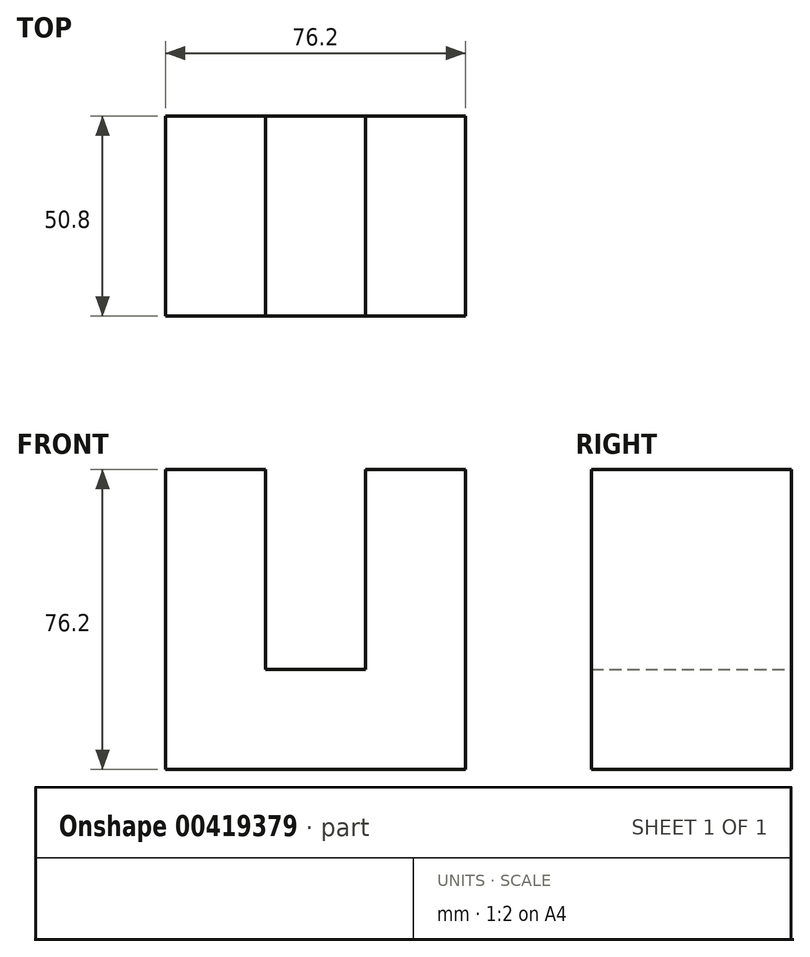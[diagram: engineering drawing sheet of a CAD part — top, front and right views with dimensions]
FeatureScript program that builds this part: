
annotation { "Feature Type Name" : "Feature", "Feature Type Description" : "" }
export const myFeature = defineFeature(function(context is Context, id is Id, definition is map)
    precondition{}
    {
        {
            var Q0;
            Q0=qCreatedBy(makeId("Front.planeOp"),FACE);
            var sketch = newSketch(context, id + "F0", { "sketchPlane" : qUnion([Q0])});
            skLineSegment(sketch, "E0", {"start": v(0, 0) * mm, "end": v(76.2, 0) * mm});
            skLineSegment(sketch, "E1", {"start": v(0, 0) * mm, "end": v(0, 76.2) * mm});
            skLineSegment(sketch, "E2", {"start": v(0, 76.2) * mm, "end": v(25.4, 76.2) * mm});
            skLineSegment(sketch, "E3", {"start": v(25.4, 76.2) * mm, "end": v(25.4, 25.4) * mm});
            skLineSegment(sketch, "E4", {"start": v(76.2, 0) * mm, "end": v(76.2, 76.2) * mm});
            skLineSegment(sketch, "E5", {"start": v(76.2, 76.2) * mm, "end": v(50.8, 76.2) * mm});
            skLineSegment(sketch, "E6", {"start": v(50.8, 76.2) * mm, "end": v(50.8, 25.4) * mm});
            skLineSegment(sketch, "E7", {"start": v(25.4, 25.4) * mm, "end": v(50.8, 25.4) * mm});
            skSolve(sketch);
        }
        {
            var Q0;
            Q0 = qSketchRegion(id + "F0", true);
            extrude(context, id + "F1", {"entities" : qUnion([Q0]), "depth" : 50.8 * mm});
        }
    });
